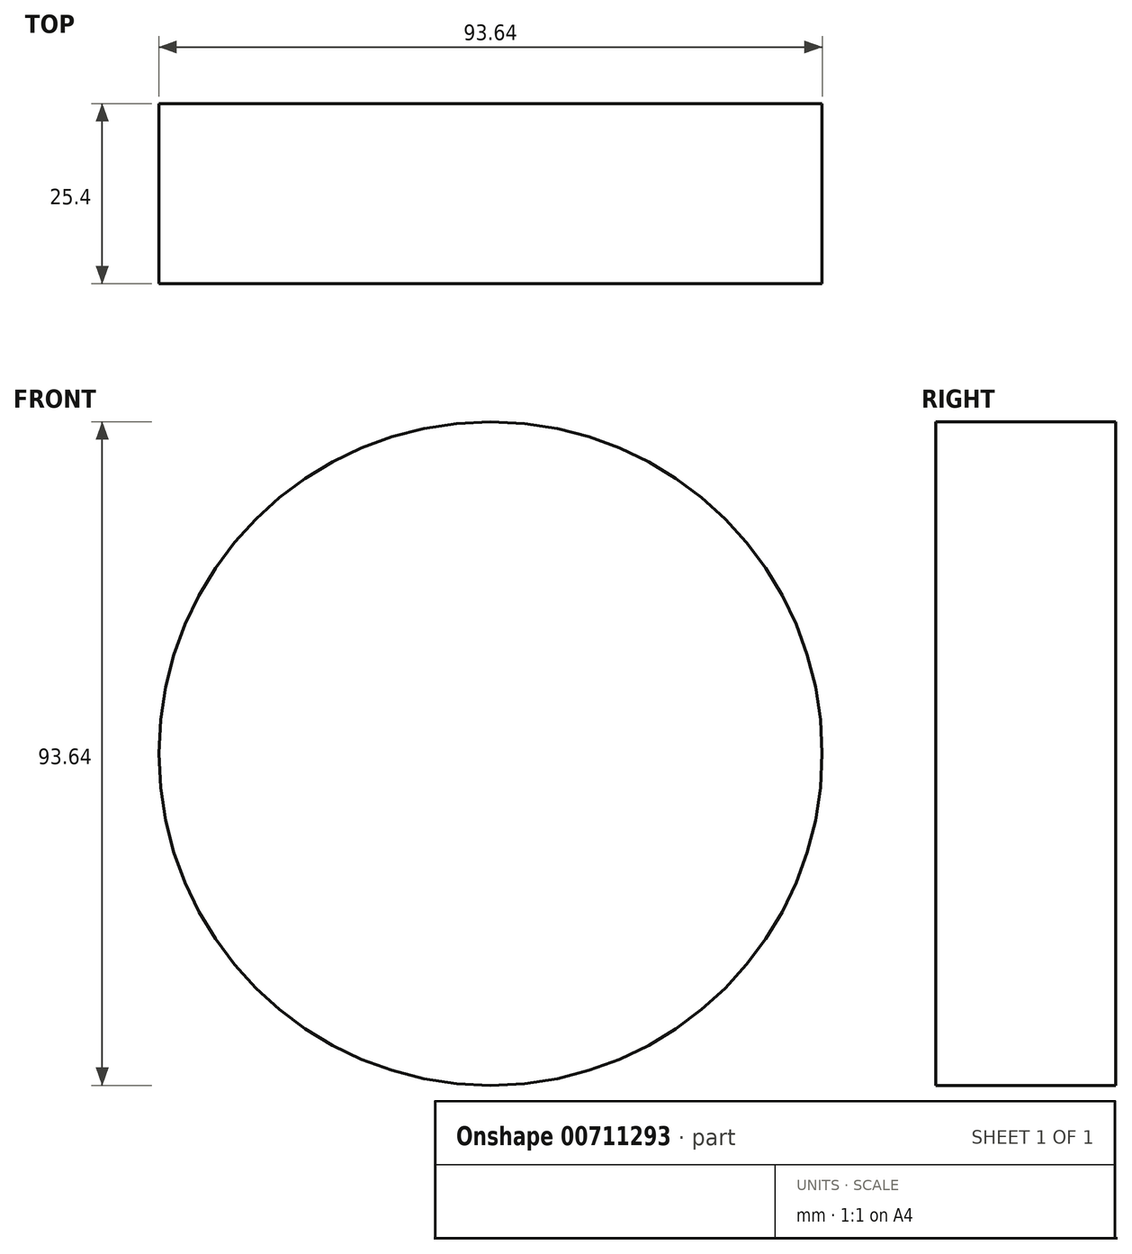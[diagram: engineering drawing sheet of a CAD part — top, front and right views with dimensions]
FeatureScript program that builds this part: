
annotation { "Feature Type Name" : "Feature", "Feature Type Description" : "" }
export const myFeature = defineFeature(function(context is Context, id is Id, definition is map)
    precondition{}
    {
        {
            var Q0;
            Q0=qCreatedBy(makeId("Front.planeOp"),FACE);
            var sketch = newSketch(context, id + "F0", { "sketchPlane" : qUnion([Q0])});
            skCircle(sketch, "E0", {"center": v(0, 0) * mm, "radius": 46.82 * mm});
            skSolve(sketch);
        }
        {
            var Q0;
            Q0=makeQuery(id+"F0.imprint","IMPRINT",FACE,{"disambiguationData":[TD([[makeQuery(id+"F0.imprint","IMPRINT",EDGE,{"derivedFrom":sQuery(id+"F0.wireOp",EDGE,"E0")}),1.0]])]});
            extrude(context, id + "F1", {"entities" : qUnion([Q0]), "depth" : 25.4 * mm, "offsetDistance" : 25.4 * mm});
        }
    });
